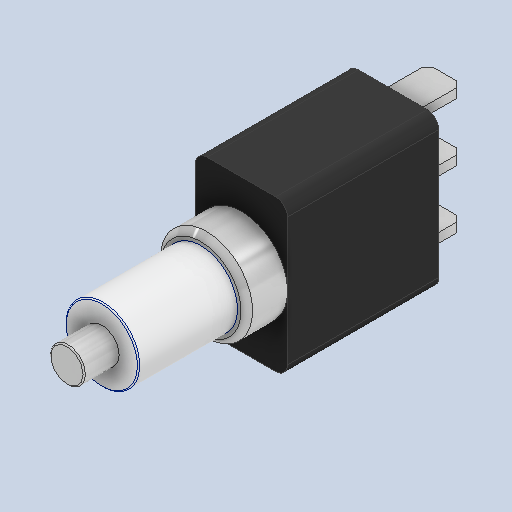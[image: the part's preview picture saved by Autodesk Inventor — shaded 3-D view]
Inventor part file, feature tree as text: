
AUTODESK INVENTOR PART (.ipt)
format: ipt  version: 2024.2 (Build 282272000, 272)  size: 226,304 bytes
history: native  units: mm
features: extrude x5, fillet x3, chamfer x2
ambient origin geometry x8: Origin, YZ Plane, XZ Plane, XY Plane, X Axis, Y Axis, Z Axis, Center Point
bodies: Solid1 (feature_tree), Solid2 (feature_tree), Solid3 (feature_tree), Solid4 (feature_tree), Solid5 (feature_tree)
feature tree (10):
  extrude  "Extrusion1"  Depth=13.0mm
  extrude  "Extrusion2"  Depth=7.9mm
  extrude  "Extrusion3"  Depth=13.0mm TaperAngle=0.0deg
  extrude  "Extrusion4"  Depth=1.5mm
  extrude  "Extrusion5"  Depth=1.5mm
  chamfer  "Chamfer1"  Distance=0.8mm
  fillet  "Fillet1"  Radius=0.8mm
  chamfer  "Chamfer2"  Distance=0.8mm
  fillet  "Fillet2"  Radius=3.0mm
  fillet  "Fillet3"  Radius=4.5mm
